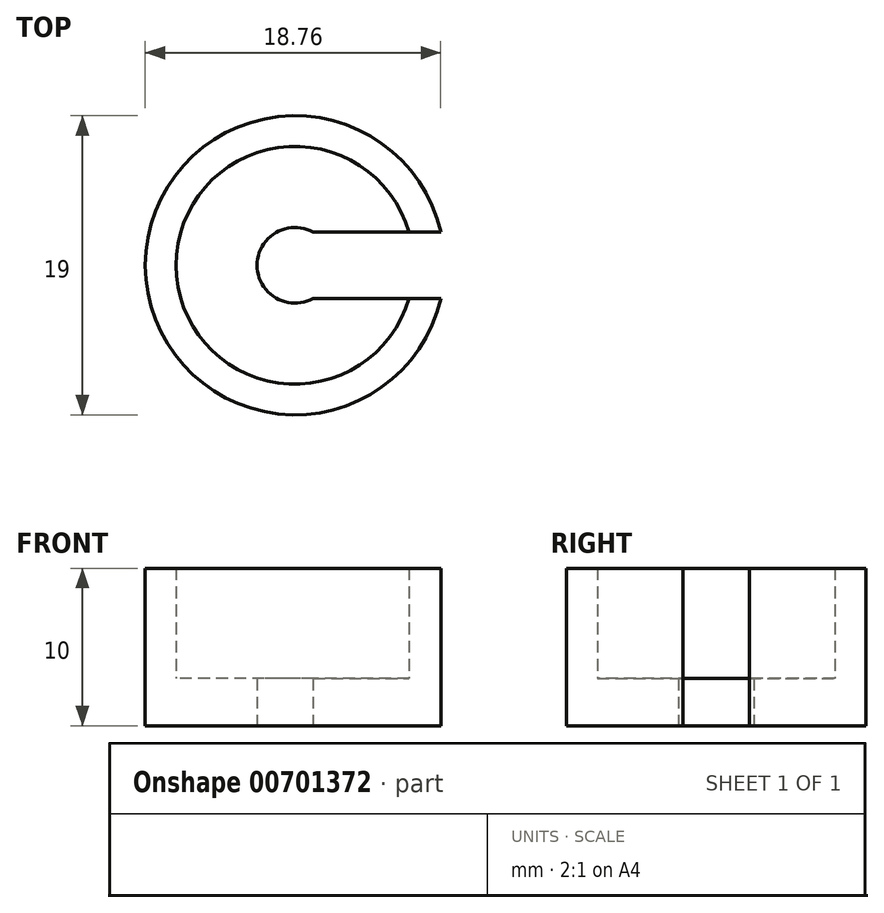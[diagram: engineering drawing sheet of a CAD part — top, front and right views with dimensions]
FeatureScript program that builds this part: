
annotation { "Feature Type Name" : "Feature", "Feature Type Description" : "" }
export const myFeature = defineFeature(function(context is Context, id is Id, definition is map)
    precondition{}
    {
        {
            var Q0;
            Q0=qCreatedBy(makeId("Top.planeOp"),FACE);
            var sketch = newSketch(context, id + "F0", { "sketchPlane" : qUnion([Q0])});
            skCircle(sketch, "E0", {"center": v(0, 0) * mm, "radius": 7.55 * mm});
            skCircle(sketch, "E1", {"center": v(0, 0) * mm, "radius": 9.5 * mm});
            skCircle(sketch, "E2", {"center": v(0, 0) * mm, "radius": 2.4 * mm});
            skCircle(sketch, "E3", {"center": v(0, 0) * mm, "radius": 2.1 * mm});
            skLineSegment(sketch, "E4.bottom", {"start": v(0, -2.1) * mm, "end": v(14, -2.1) * mm});
            skLineSegment(sketch, "E4.top", {"start": v(0, 2.1) * mm, "end": v(14, 2.1) * mm});
            skLineSegment(sketch, "E4.left", {"start": v(0, -2.1) * mm, "end": v(0, 2.1) * mm});
            skLineSegment(sketch, "E4.right", {"start": v(14, -2.1) * mm, "end": v(14, 2.1) * mm});
            skSolve(sketch);
        }
        {
            var Q0;
            {var subQ0=sQuery(id+"F0.wireOp",EDGE,"E4.bottom");var subQ1=sQuery(id+"F0.wireOp",EDGE,"E0");var subQ2=makeQuery(id+"F0.imprint","INTERSECT",VERTEX,{"derivedFrom":[subQ1,subQ0]});Q0=makeQuery(id+"F0.imprint","IMPRINT",FACE,{"disambiguationData":[TD([[makeQuery(id+"F0.imprint","IMPRINT",EDGE,{"disambiguationData":[TD([[subQ2,1.0]])],"derivedFrom":subQ1}),-1.0]])]});}
            extrude(context, id + "F1", {"entities" : qUnion([Q0]), "depth" : 10 * mm, "offsetDistance" : 25 * mm});
        }
        {
            var Q0;
            {var subQ0=sQuery(id+"F0.wireOp",EDGE,"E4.bottom");var subQ1=sQuery(id+"F0.wireOp",EDGE,"E0");var subQ2=makeQuery(id+"F0.imprint","INTERSECT",VERTEX,{"derivedFrom":[subQ1,subQ0]});Q0=makeQuery(id+"F0.imprint","IMPRINT",FACE,{"disambiguationData":[TD([[makeQuery(id+"F0.imprint","IMPRINT",EDGE,{"disambiguationData":[TD([[subQ2,1.0]])],"derivedFrom":subQ1}),1.0]])]});}
            extrude(context, id + "F2", {"entities" : qUnion([Q0]), "operationType" : NewBodyOperationType.ADD, "depth" : 3 * mm, "offsetDistance" : 25 * mm});
        }
    });
